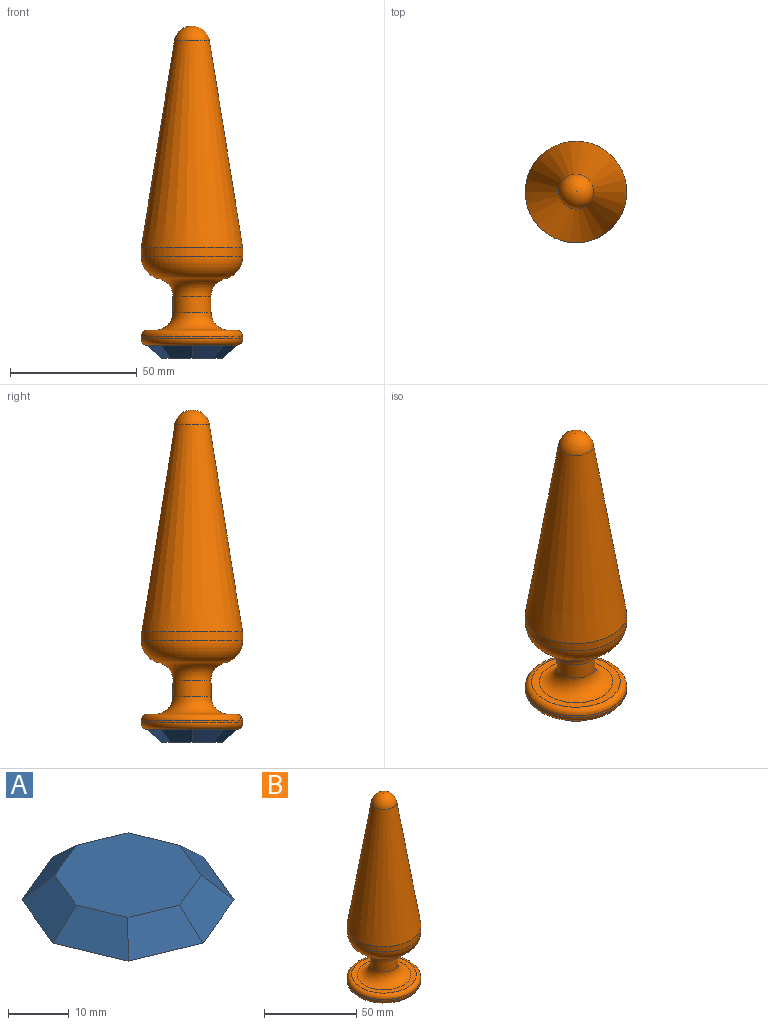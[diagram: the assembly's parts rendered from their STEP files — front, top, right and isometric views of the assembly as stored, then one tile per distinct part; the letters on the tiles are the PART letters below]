
ASSEMBLY  parts=2 mates=1
PART A: 13 faces, bbox 35x35x9.5 mm
  f0: plane 24.18x24.18mm, normal (0,0,1), area 413.3mm2, adj f2,f3,f4,f5,f6,f7,f8,f9
  f1: plane 35x35mm, normal (0,0,-1), area 848.1mm2, adj f2,f3,f4,f5,f6,f7,f8,f9
  f2: plane 12.37x8.95mm, normal (0.27,-0.65,0.71), area 80.1mm2, adj f0,f1,f3,f4
  f3: plane 12.37x8.95mm, normal (-0.27,-0.65,0.71), area 80.1mm2, adj f0,f1,f2,f5
  f4: plane 12.37x8.95mm, normal (0.65,-0.27,0.71), area 80.1mm2, adj f0,f1,f2,f6
  f5: plane 12.37x8.95mm, normal (-0.65,-0.27,0.71), area 80.1mm2, adj f0,f1,f3,f7
  f6: plane 12.37x8.95mm, normal (0.65,0.27,0.71), area 80.1mm2, adj f0,f1,f4,f8
  f7: plane 12.37x8.95mm, normal (-0.65,0.27,0.71), area 80.1mm2, adj f0,f1,f5,f9
  f8: plane 12.37x8.95mm, normal (0.27,0.65,0.71), area 80.1mm2, adj f0,f1,f6,f9
  f9: plane 12.37x8.95mm, normal (-0.27,0.65,0.71), area 80.1mm2, adj f0,f1,f7,f8
  f10: cylinder r=2.4mm len=4.8mm, axis (0,0,1), area 60.3mm2, adj f1,f12
  f11: plane 3.8x3.8mm, normal (0,0,-1), area 11.3mm2, adj f12
  f12: cone r=1.9mm half-angle=45deg, axis (0,0,1), area 9.6mm2, adj f10,f11
PART B: 15 faces, bbox 43.3x43.3x126 mm
  f0: plane 35x35mm, normal (0,0,-1), area 933.8mm2, adj f10,f14
  f1: cylinder r=20mm len=40mm, axis (0,0,-1), area 125.7mm2, adj f10,f11
  f2: plane 35x35mm, normal (0,0,1), area 301.6mm2, adj f8,f11
  f3: cylinder r=7.5mm len=15mm, axis (0,0,-1), area 301mm2, adj f8,f9
  f4: cylinder r=20mm len=40mm, axis (0,0,-1), area 439.8mm2, adj f5,f7
  f5: cone r=6.91mm half-angle=9.1deg, axis (0,0,-1), area 6987.8mm2, adj f4,f6
  f6: sphere r=7mm, area 259.1mm2, adj f5
  f7: torus R=11mm, axis (0,0,-1), area 1336.5mm2, adj f4,f9
  f8: torus R=14.5mm, axis (0,0,1), area 693.9mm2, adj f2,f3
  f9: torus R=14.5mm, axis (0,0,-1), area 560.7mm2, adj f3,f7
  f10: torus R=17.5mm, axis (0,0,-1), area 471.1mm2, adj f0,f1
  f11: torus R=17.5mm, axis (0,0,1), area 471.1mm2, adj f1,f2
  f12: cylinder r=2.5mm len=5mm, axis (0,0,-1), area 70.7mm2, adj f13,f14
  f13: plane 5x5mm, normal (0,0,-1), area 19.6mm2, adj f12
  f14: cone r=2.5mm half-angle=45deg, axis (0,0,-1), area 12.2mm2, adj f0,f12
PLACE A rot(axis=(1,0,0),180deg) t=(-26.48,25.86,-1.28)mm
PLACE B t=(-26.48,25.86,-1.28)mm
MATE revolute A.f10 <-> B.f12  axis (0,0,1) through (-26.48,25.86,-1.28)mm
